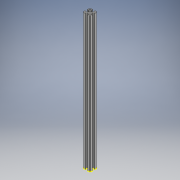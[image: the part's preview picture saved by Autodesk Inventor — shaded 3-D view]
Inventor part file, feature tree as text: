
AUTODESK INVENTOR PART (.ipt)
format: ipt  version: 2018.3 (Build 223284000, 284)  size: 673,280 bytes
history: native  units: mm
features: sketch x4, projected_geometry x4, extrude x3, plane x1, fillet x1
ambient origin geometry x8: Origin, YZ Plane, XZ Plane, XY Plane, X Axis, Y Axis, Z Axis, Center Point
bodies: Solid1 (feature_tree)
feature tree (13):
  sketch  "Sketch1"  dims[d0=10.0mm d1=0.0mm d2=165.1mm d3=0.0mm]
  plane  "Work Plane1"
  extrude  "Extrusion1"  Depth=165.1mm TaperAngle=0.0deg
  sketch  "Sketch2"  dims[d4=6.35mm d5=0.0mm]
  extrude  "Extrusion2"  [1 undecoded]
  extrude  "Extrusion3"  [1 undecoded]
  projected_geometry  "Projected Loop1"
  projected_geometry  "Projected Loop2"
  sketch  "Sketch3"
  projected_geometry  "Projected Loop3"
  sketch  "Sketch4"
  projected_geometry  "Projected Loop4"
  fillet  "Fillet6"  [1 undecoded]
note: 3 required parameter values undecoded (feature->parameter linkage not recoverable at this tier; creation-order binding heuristic only, values carry confidence <= 0.55)
